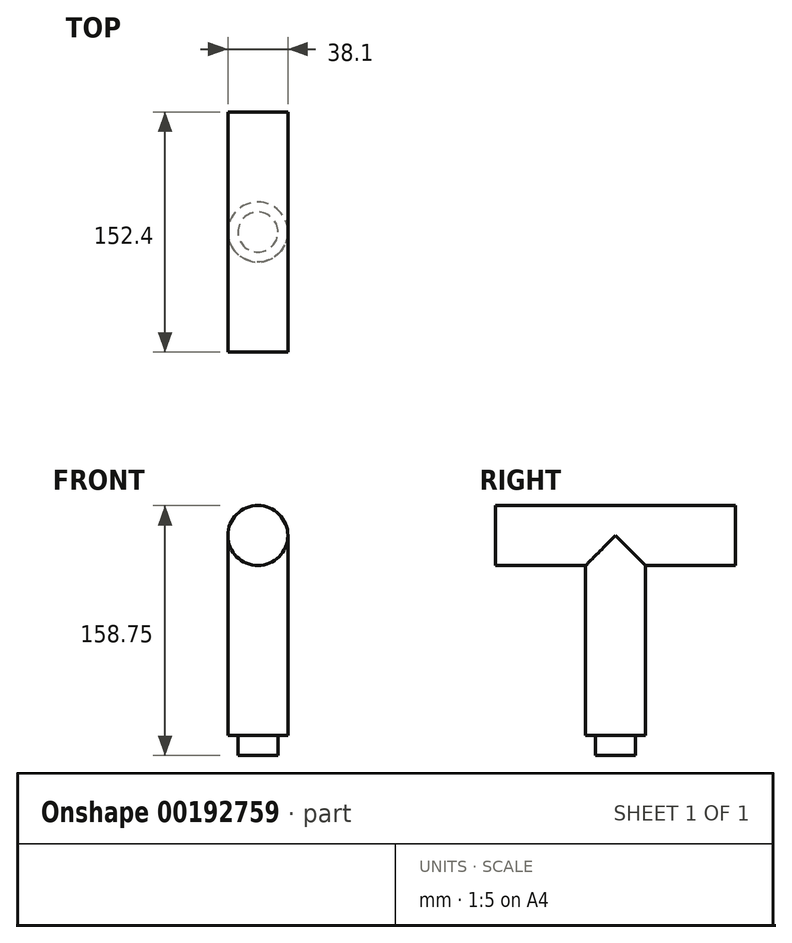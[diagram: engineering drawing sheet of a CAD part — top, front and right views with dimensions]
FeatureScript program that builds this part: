
annotation { "Feature Type Name" : "Feature", "Feature Type Description" : "" }
export const myFeature = defineFeature(function(context is Context, id is Id, definition is map)
    precondition{}
    {
        {
            var Q0;
            Q0=qCreatedBy(makeId("Top.planeOp"),FACE);
            var sketch = newSketch(context, id + "F0", { "sketchPlane" : qUnion([Q0])});
            skCircle(sketch, "E0", {"center": v(0, 0) * mm, "radius": 19.05 * mm});
            skSolve(sketch);
        }
        {
            var Q0;
            Q0=makeQuery(id+"F0.imprint","IMPRINT",FACE,{"disambiguationData":[TD([[makeQuery(id+"F0.imprint","IMPRINT",EDGE,{"derivedFrom":sQuery(id+"F0.wireOp",EDGE,"E0")}),1.0]])]});
            extrude(context, id + "F1", {"entities" : qUnion([Q0]), "depth" : 127 * mm});
        }
        {
            var Q0;
            Q0=makeQuery(id+"F1.opExtrude","CAP_FACE",FACE,{"disambiguationData":[OSD([sQuery(id+"F0.wireOp",EDGE,"E0")])],"isStart":true});
            var sketch = newSketch(context, id + "F2", { "sketchPlane" : qUnion([Q0])});
            skCircle(sketch, "E1", {"center": v(0, 0) * mm, "radius": 12.7 * mm});
            skSolve(sketch);
        }
        {
            var Q0;
            Q0 = qSketchRegion(id + "F2", true);
            extrude(context, id + "F3", {"entities" : qUnion([Q0]), "operationType" : NewBodyOperationType.ADD, "depth" : 12.7 * mm});
        }
        {
            var Q0;
            Q0=qCreatedBy(makeId("Front.planeOp"),FACE);
            var sketch = newSketch(context, id + "F4", { "sketchPlane" : qUnion([Q0])});
            skLineSegment(sketch, "E2", {"start": v(0, 0) * mm, "end": v(0, 127) * mm, "construction": true});
            skSolve(sketch);
        }
        {
            var Q0;
            Q0=sQuery(id+"F4.wireOp",EDGE,"E2");
            cPlane(context, id + "F5", {"entities" : qUnion([Q0]), "cplaneType" : CPlaneType.LINE_ANGLE, "offset" : 25.4 * mm, "angle" : 90 * degree, "width" : 152.4 * mm, "height" : 152.4 * mm});
        }
        {
            var Q0;
            Q0=qCreatedBy(id+"F5.planeOp",FACE);
            var sketch = newSketch(context, id + "F6", { "sketchPlane" : qUnion([Q0])});
            skCircle(sketch, "E3", {"center": v(0, 127) * mm, "radius": 19.05 * mm});
            skSolve(sketch);
        }
        {
            var Q0;
            Q0=makeQuery(id+"F6.imprint","IMPRINT",FACE,{"disambiguationData":[TD([[makeQuery(id+"F6.imprint","IMPRINT",EDGE,{"derivedFrom":sQuery(id+"F6.wireOp",EDGE,"E3")}),1.0]])]});
            extrude(context, id + "F7", {"entities" : qUnion([Q0]), "operationType" : NewBodyOperationType.ADD, "depth" : 76.2 * mm, "hasSecondDirection" : true, "secondDirectionOppositeDirection" : true, "secondDirectionDepth" : 76.2 * mm});
        }
    });
